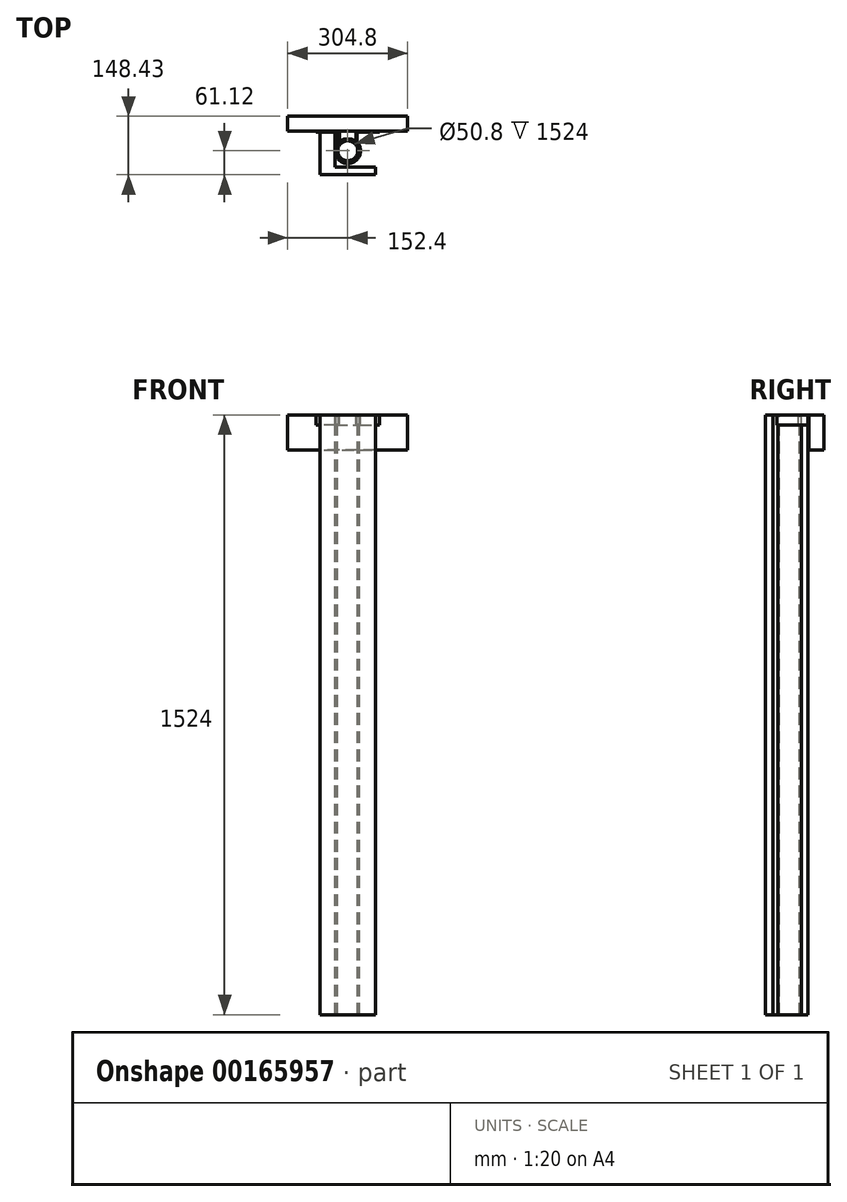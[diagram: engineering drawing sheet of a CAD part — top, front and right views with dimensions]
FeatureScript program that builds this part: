
annotation { "Feature Type Name" : "Feature", "Feature Type Description" : "" }
export const myFeature = defineFeature(function(context is Context, id is Id, definition is map)
    precondition{}
    {
        {
            var Q0;
            Q0=qCreatedBy(makeId("Top.planeOp"),FACE);
            var sketch = newSketch(context, id + "F0", { "sketchPlane" : qUnion([Q0])});
            skCircle(sketch, "E0", {"center": v(0, 0) * mm, "radius": 30.16 * mm});
            skCircle(sketch, "E1", {"center": v(0, 0) * mm, "radius": 25.4 * mm});
            skLineSegment(sketch, "E2", {"start": v(-152.4, -30.16) * mm, "end": v(152.4, -30.16) * mm, "construction": true});
            skLineSegment(sketch, "E3", {"start": v(27.38, 49.21) * mm, "end": v(80.96, 49.21) * mm});
            skLineSegment(sketch, "E4.0", {"start": v(29.77, 46.83) * mm, "end": v(80.96, 46.83) * mm});
            skLineSegment(sketch, "E5", {"start": v(21.03, 42.86) * mm, "end": v(21.03, 21.62) * mm});
            skLineSegment(sketch, "E6", {"start": v(23.42, 40.48) * mm, "end": v(23.42, 25.03) * mm});
            skPoint(sketch, "E7.newPointB", {"position": v(21.03, 49.21) * mm});
            skArc(sketch, "E7.filletArc", {"start": v(27.38, 49.21) * mm, "mid": v(22.9, 47.35) * mm, "end": v(21.03, 42.86) * mm});
            skPoint(sketch, "E8.newPointB", {"position": v(23.42, 46.83) * mm});
            skArc(sketch, "E8.filletArc", {"start": v(29.77, 46.83) * mm, "mid": v(25.28, 44.97) * mm, "end": v(23.42, 40.48) * mm});
            skLineSegment(sketch, "E9", {"start": v(80.96, 49.21) * mm, "end": v(80.96, 46.83) * mm});
            skLineSegment(sketch, "E10.MirrorCS", {"start": v(-80.96, 49.21) * mm, "end": v(-80.96, 46.83) * mm});
            skArc(sketch, "E11.MirrorCS", {"start": v(-27.38, 49.21) * mm, "mid": v(-22.9, 47.35) * mm, "end": v(-21.03, 42.86) * mm});
            skArc(sketch, "E12.MirrorCS", {"start": v(-29.77, 46.83) * mm, "mid": v(-25.28, 44.97) * mm, "end": v(-23.42, 40.48) * mm});
            skPoint(sketch, "E13.MirrorP", {"position": v(-23.42, 46.83) * mm});
            skLineSegment(sketch, "E14.MirrorCS", {"start": v(-21.03, 42.86) * mm, "end": v(-21.03, 21.62) * mm});
            skPoint(sketch, "E15.MirrorP", {"position": v(-21.03, 49.21) * mm});
            skLineSegment(sketch, "E16.MirrorCS", {"start": v(-27.38, 49.21) * mm, "end": v(-80.96, 49.21) * mm});
            skLineSegment(sketch, "E17.MirrorCS", {"start": v(-29.77, 46.83) * mm, "end": v(-80.96, 46.83) * mm});
            skLineSegment(sketch, "E18.MirrorCS", {"start": v(-23.42, 40.48) * mm, "end": v(-23.42, 25.03) * mm});
            skArc(sketch, "E19.trimOffspring", {"start": v(-24.9, 20.95) * mm, "mid": v(0, -32.54) * mm, "end": v(24.9, 20.95) * mm});
            skPoint(sketch, "E20.visualSharp", {"position": v(-23.42, 22.6) * mm});
            skArc(sketch, "E20.filletArc", {"start": v(-24.9, 20.95) * mm, "mid": v(-23.8, 22.86) * mm, "end": v(-23.42, 25.03) * mm});
            skPoint(sketch, "E21.visualSharp", {"position": v(23.42, 22.6) * mm});
            skArc(sketch, "E21.filletArc", {"start": v(23.42, 25.03) * mm, "mid": v(23.8, 22.86) * mm, "end": v(24.9, 20.95) * mm});
            skLineSegment(sketch, "E22.bottom", {"start": v(32.54, 46.83) * mm, "end": v(70.64, 46.83) * mm});
            skLineSegment(sketch, "E22.top", {"start": v(32.54, -42.07) * mm, "end": v(70.64, -42.07) * mm});
            skLineSegment(sketch, "E22.left", {"start": v(32.54, 46.83) * mm, "end": v(32.54, -42.07) * mm});
            skLineSegment(sketch, "E22.right", {"start": v(70.64, 46.83) * mm, "end": v(70.64, -42.07) * mm});
            skLineSegment(sketch, "E23.MirrorCS", {"start": v(-32.54, -42.07) * mm, "end": v(-70.64, -42.07) * mm});
            skLineSegment(sketch, "E24.MirrorCS", {"start": v(-32.54, 46.83) * mm, "end": v(-32.54, -42.07) * mm});
            skLineSegment(sketch, "E25.MirrorCS", {"start": v(-70.64, 46.83) * mm, "end": v(-70.64, -42.07) * mm});
            skLineSegment(sketch, "E26.MirrorCS", {"start": v(-32.54, 46.83) * mm, "end": v(-70.64, 46.83) * mm});
            skLineSegment(sketch, "E27.bottom", {"start": v(-70.64, -42.07) * mm, "end": v(70.58, -42.07) * mm});
            skLineSegment(sketch, "E27.top", {"start": v(-70.64, -61.12) * mm, "end": v(70.58, -61.12) * mm});
            skLineSegment(sketch, "E27.left", {"start": v(-70.64, -42.07) * mm, "end": v(-70.64, -61.12) * mm});
            skLineSegment(sketch, "E27.right", {"start": v(70.58, -42.07) * mm, "end": v(70.58, -61.12) * mm});
            skLineSegment(sketch, "E28.bottom", {"start": v(-152.4, 87.31) * mm, "end": v(152.4, 87.31) * mm});
            skLineSegment(sketch, "E28.top", {"start": v(-152.4, 49.21) * mm, "end": v(152.4, 49.21) * mm});
            skLineSegment(sketch, "E28.left", {"start": v(-152.4, 87.31) * mm, "end": v(-152.4, 49.21) * mm});
            skLineSegment(sketch, "E28.right", {"start": v(152.4, 87.31) * mm, "end": v(152.4, 49.21) * mm});
            skSolve(sketch);
        }
        {
            var Q0;
            {var subQ1=sQuery(id+"F0.wireOp",EDGE,"E25.MirrorCS");Q0=makeQuery(id+"F0.imprint","IMPRINT",FACE,{"disambiguationData":[TD([[makeQuery(id+"F0.imprint","IMPRINT",EDGE,{"derivedFrom":subQ1}),1.0]])]});}
            var Q1;
            {var subQ4=sQuery(id+"F0.wireOp",EDGE,"E22.bottom");Q1=makeQuery(id+"F0.imprint","IMPRINT",FACE,{"disambiguationData":[TD([[makeQuery(id+"F0.imprint","IMPRINT",EDGE,{"derivedFrom":subQ4}),-1.0]])]});}
            var Q2;
            Q2=makeQuery(id+"F0.imprint","IMPRINT",FACE,{"disambiguationData":[TD([[makeQuery(id+"F0.imprint","IMPRINT",EDGE,{"derivedFrom":sQuery(id+"F0.wireOp",EDGE,"E27.top")}),1.0]])]});
            var Q3;
            Q3=makeQuery(id+"F0.imprint","IMPRINT",FACE,{"disambiguationData":[TD([[makeQuery(id+"F0.imprint","IMPRINT",EDGE,{"derivedFrom":sQuery(id+"F0.wireOp",EDGE,"E1")}),-1.0]])]});
            extrude(context, id + "F1", {"entities" : qUnion([Q0, Q1, Q2, Q3]), "oppositeDirection" : true, "depth" : 1524 * mm});
        }
        {
            var Q0;
            {var subQ8=sQuery(id+"F0.wireOp",EDGE,"E5");Q0=makeQuery(id+"F0.imprint","IMPRINT",FACE,{"disambiguationData":[TD([[makeQuery(id+"F0.imprint","IMPRINT",EDGE,{"derivedFrom":subQ8}),1.0]])]});}
            extrude(context, id + "F2", {"entities" : qUnion([Q0]), "oppositeDirection" : true, "depth" : 25.4 * mm});
        }
        {
            var Q0;
            Q0=makeQuery(id+"F0.imprint","IMPRINT",FACE,{"disambiguationData":[TD([[makeQuery(id+"F0.imprint","IMPRINT",EDGE,{"derivedFrom":sQuery(id+"F0.wireOp",EDGE,"E28.bottom")}),-1.0]])]});
            extrude(context, id + "F3", {"entities" : qUnion([Q0]), "oppositeDirection" : true, "depth" : 88.9 * mm});
        }
    });
